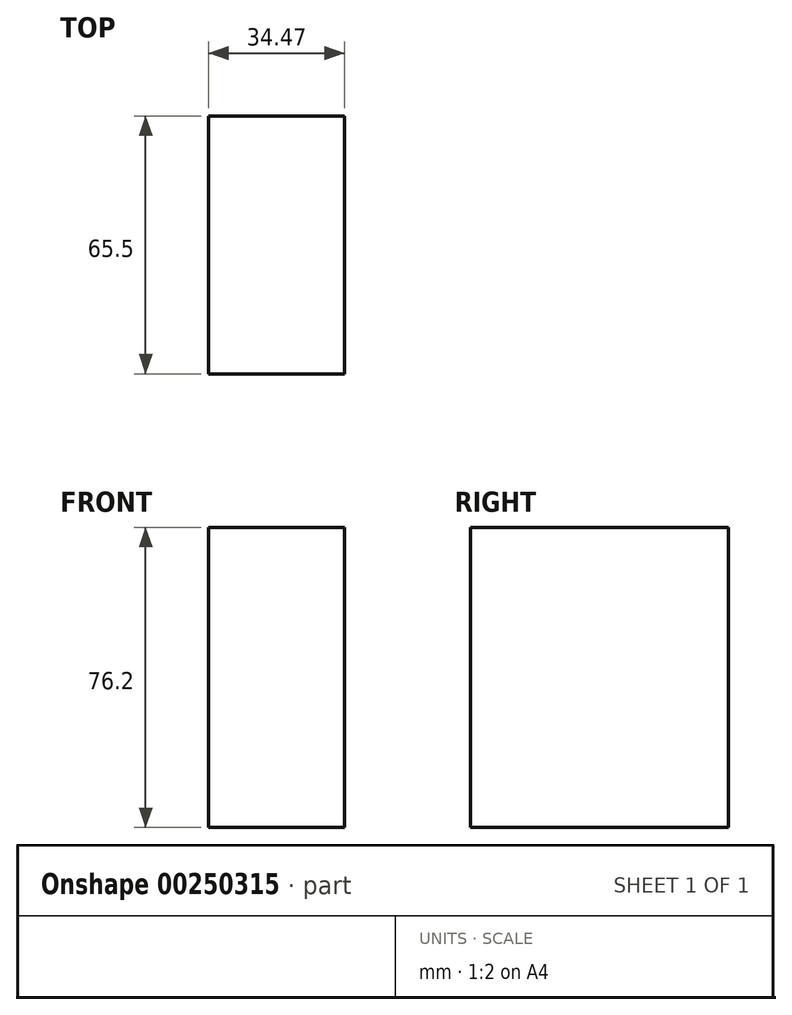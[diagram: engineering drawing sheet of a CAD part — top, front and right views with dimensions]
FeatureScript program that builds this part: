
annotation { "Feature Type Name" : "Feature", "Feature Type Description" : "" }
export const myFeature = defineFeature(function(context is Context, id is Id, definition is map)
    precondition{}
    {
        {
            var Q0;
            Q0=qCreatedBy(makeId("Top.planeOp"),FACE);
            var sketch = newSketch(context, id + "F0", { "sketchPlane" : qUnion([Q0])});
            skLineSegment(sketch, "E0.bottom", {"start": v(-417.37, -204.51) * mm, "end": v(-382.9, -204.51) * mm});
            skLineSegment(sketch, "E0.top", {"start": v(-417.37, -139) * mm, "end": v(-382.9, -139) * mm});
            skLineSegment(sketch, "E0.left", {"start": v(-417.37, -204.51) * mm, "end": v(-417.37, -139) * mm});
            skLineSegment(sketch, "E0.right", {"start": v(-382.9, -204.51) * mm, "end": v(-382.9, -139) * mm});
            skSolve(sketch);
        }
        {
            var Q0;
            Q0=makeQuery(id+"F0.imprint","IMPRINT",FACE,{"disambiguationData":[TD([[makeQuery(id+"F0.imprint","IMPRINT",EDGE,{"derivedFrom":sQuery(id+"F0.wireOp",EDGE,"E0.bottom")}),1.0]])]});
            extrude(context, id + "F1", {"entities" : qUnion([Q0]), "depth" : 76.2 * mm});
        }
    });
